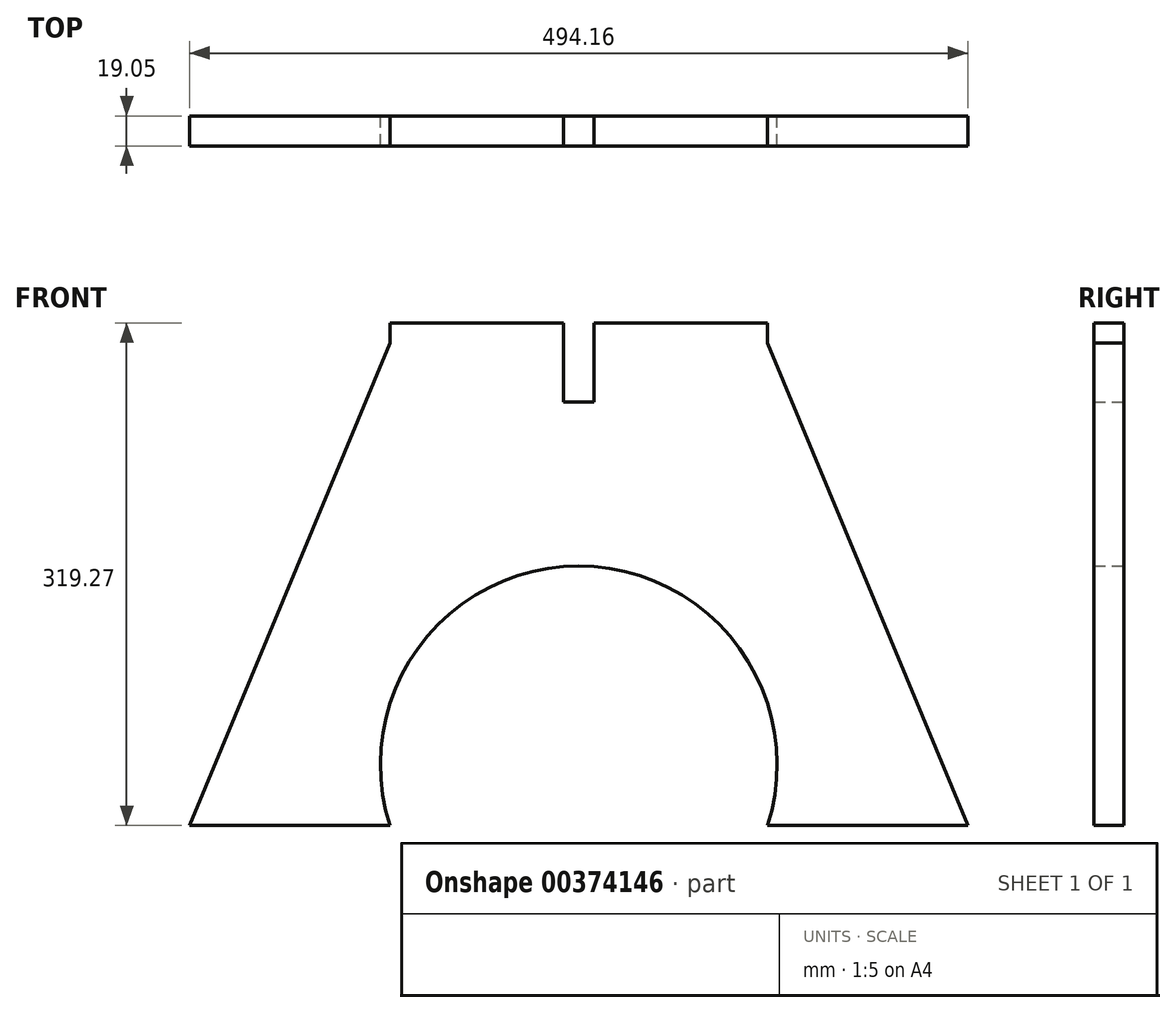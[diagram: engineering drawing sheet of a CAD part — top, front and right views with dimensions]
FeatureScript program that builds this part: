
annotation { "Feature Type Name" : "Feature", "Feature Type Description" : "" }
export const myFeature = defineFeature(function(context is Context, id is Id, definition is map)
    precondition{}
    {
        {
            var Q0;
            Q0=qCreatedBy(makeId("Front.planeOp"),FACE);
            var sketch = newSketch(context, id + "F0", { "sketchPlane" : qUnion([Q0])});
            skLineSegment(sketch, "E0", {"start": v(0, 155.77) * mm, "end": v(119.89, 155.77) * mm});
            skLineSegment(sketch, "E1", {"start": v(0, 155.77) * mm, "end": v(-119.89, 155.77) * mm});
            skLineSegment(sketch, "E2", {"start": v(247.08, -163.5) * mm, "end": v(119.89, -163.5) * mm});
            skLineSegment(sketch, "E3", {"start": v(0, 155.77) * mm, "end": v(0, 7.25) * mm, "construction": true});
            skLineSegment(sketch, "E4.MirrorCS", {"start": v(-247.08, -163.5) * mm, "end": v(-119.89, -163.5) * mm});
            skPoint(sketch, "E5.third.point", {"position": v(-119.89, -77.29) * mm});
            skLineSegment(sketch, "E6.trimOffspring", {"start": v(0, -115.14) * mm, "end": v(0, -120.4) * mm, "construction": true});
            skLineSegment(sketch, "E7", {"start": v(119.89, 155.77) * mm, "end": v(119.89, 143.07) * mm});
            skLineSegment(sketch, "E8", {"start": v(119.89, 143.07) * mm, "end": v(247.08, -163.5) * mm});
            skLineSegment(sketch, "E9", {"start": v(-119.89, 155.77) * mm, "end": v(-119.89, 143.07) * mm});
            skLineSegment(sketch, "E10", {"start": v(-119.89, 143.07) * mm, "end": v(-247.08, -163.5) * mm});
            skArc(sketch, "E11", {"start": v(119.89, -163.5) * mm, "mid": v(0, 1.38) * mm, "end": v(-119.89, -163.5) * mm});
            skPoint(sketch, "E11.third.point", {"position": v(-18.57, 0) * mm});
            skSolve(sketch);
        }
        {
            var Q0;
            Q0=qSketchRegion(id+"F0",true);
            extrude(context, id + "F1", {"entities" : qUnion([Q0]), "depth" : 19.05 * mm});
        }
        {
            var Q0;
            Q0=qCreatedBy(makeId("Front.planeOp"),FACE);
            var sketch = newSketch(context, id + "F2", { "sketchPlane" : qUnion([Q0])});
            skLineSegment(sketch, "E12", {"start": v(0, 0) * mm, "end": v(0, 105.58) * mm, "construction": true});
            skLineSegment(sketch, "E13", {"start": v(0, 105.58) * mm, "end": v(-9.78, 105.58) * mm});
            skLineSegment(sketch, "E14", {"start": v(0, 105.58) * mm, "end": v(0, 157.41) * mm, "construction": true});
            skLineSegment(sketch, "E15.MirrorCS", {"start": v(0, 105.58) * mm, "end": v(9.78, 105.58) * mm});
            skLineSegment(sketch, "E16", {"start": v(9.78, 105.58) * mm, "end": v(9.78, 155.77) * mm});
            skLineSegment(sketch, "E17", {"start": v(9.78, 155.77) * mm, "end": v(0, 155.77) * mm});
            skLineSegment(sketch, "E18.MirrorCS", {"start": v(-9.78, 105.58) * mm, "end": v(-9.78, 155.77) * mm});
            skLineSegment(sketch, "E19.MirrorCS", {"start": v(-9.78, 155.77) * mm, "end": v(0, 155.77) * mm});
            skSolve(sketch);
        }
        {
            var Q0;
            Q0=qSketchRegion(id+"F2",true);
            extrude(context, id + "F3", {"entities" : qUnion([Q0]), "operationType" : NewBodyOperationType.REMOVE, "depth" : 19.05 * mm});
        }
    });
